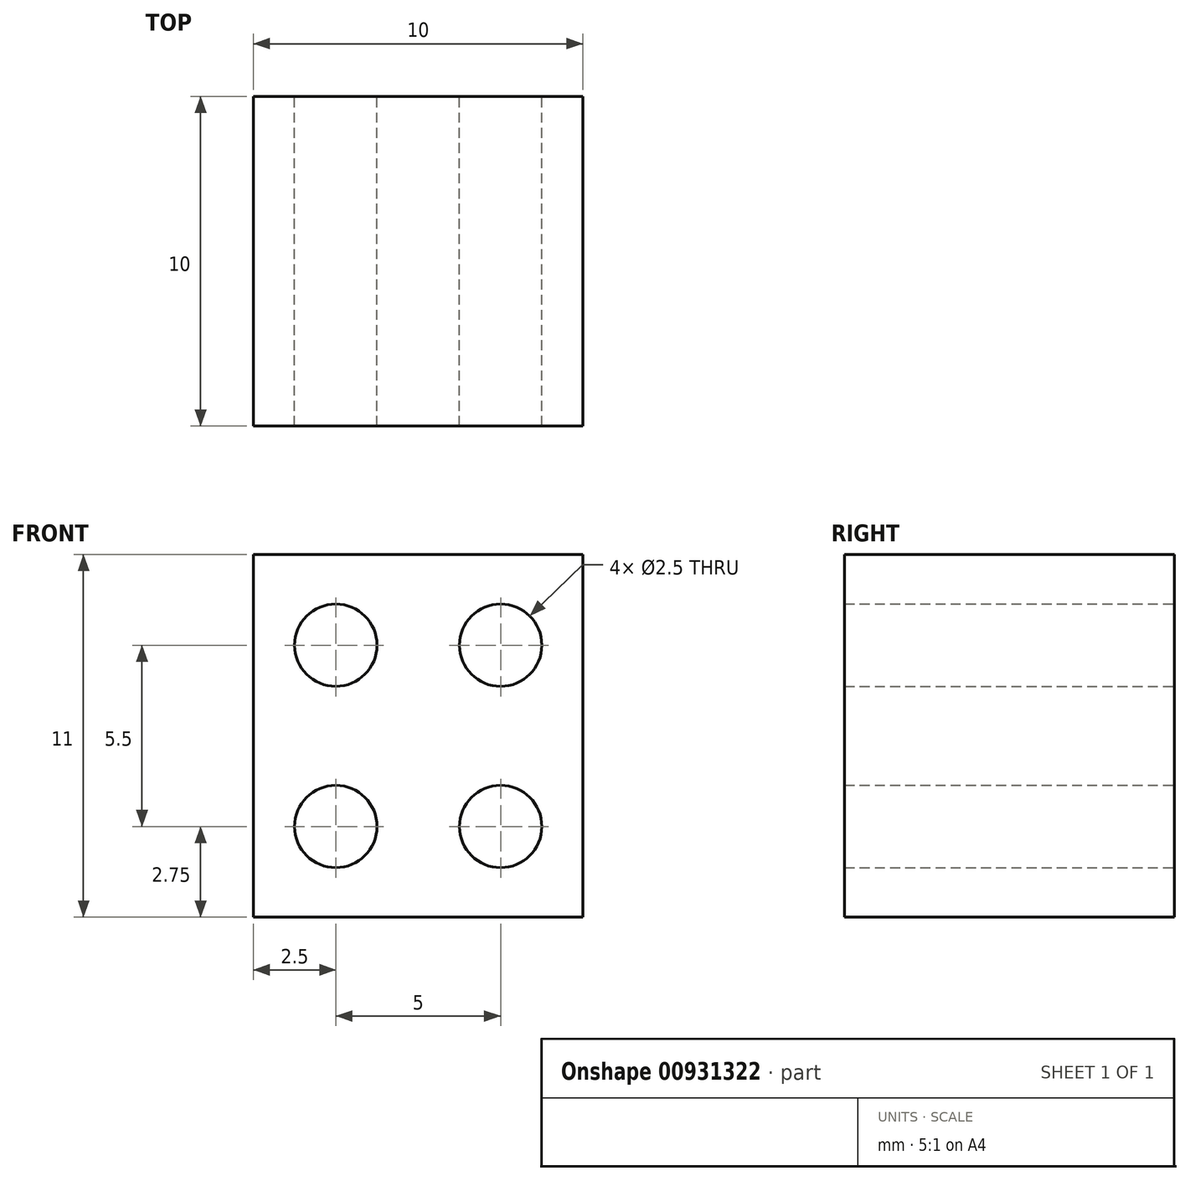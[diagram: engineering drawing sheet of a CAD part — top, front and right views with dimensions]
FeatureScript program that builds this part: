
annotation { "Feature Type Name" : "Feature", "Feature Type Description" : "" }
export const myFeature = defineFeature(function(context is Context, id is Id, definition is map)
    precondition{}
    {
        {
            var Q0;
            Q0=qCreatedBy(makeId("Front.planeOp"),FACE);
            var sketch = newSketch(context, id + "F0", { "sketchPlane" : qUnion([Q0])});
            skLineSegment(sketch, "E0.bottom", {"start": v(-5, 5.5) * mm, "end": v(5, 5.5) * mm});
            skLineSegment(sketch, "E0.top", {"start": v(-5, -5.5) * mm, "end": v(5, -5.5) * mm});
            skLineSegment(sketch, "E0.left", {"start": v(-5, 5.5) * mm, "end": v(-5, -5.5) * mm});
            skLineSegment(sketch, "E0.right", {"start": v(5, 5.5) * mm, "end": v(5, -5.5) * mm});
            skPoint(sketch, "E0.middle", {"position": v(0, 0) * mm});
            skPoint(sketch, "E1", {"position": v(0, 5.5) * mm});
            skPoint(sketch, "E2", {"position": v(-5, 0) * mm});
            skPoint(sketch, "E3", {"position": v(0, -5.5) * mm});
            skPoint(sketch, "E4", {"position": v(5, 0) * mm});
            skPoint(sketch, "E5", {"position": v(-2.5, 2.75) * mm});
            skPoint(sketch, "E6", {"position": v(2.5, 2.75) * mm});
            skPoint(sketch, "E7", {"position": v(2.5, -2.75) * mm});
            skPoint(sketch, "E8", {"position": v(-2.5, -2.75) * mm});
            skCircle(sketch, "E9", {"center": v(-2.5, 2.75) * mm, "radius": 1.25 * mm});
            skCircle(sketch, "E10", {"center": v(2.5, 2.75) * mm, "radius": 1.25 * mm});
            skCircle(sketch, "E11", {"center": v(-2.5, -2.75) * mm, "radius": 1.25 * mm});
            skCircle(sketch, "E12", {"center": v(2.5, -2.75) * mm, "radius": 1.25 * mm});
            skSolve(sketch);
        }
        {
            var Q0;
            Q0=makeQuery(id+"F0.imprint","IMPRINT",FACE,{"disambiguationData":[TD([[makeQuery(id+"F0.imprint","IMPRINT",EDGE,{"derivedFrom":sQuery(id+"F0.wireOp",EDGE,"E0.bottom")}),-1.0]])]});
            extrude(context, id + "F1", {"entities" : qUnion([Q0]), "depth" : 10 * mm, "offsetDistance" : 25.4 * mm});
        }
    });
